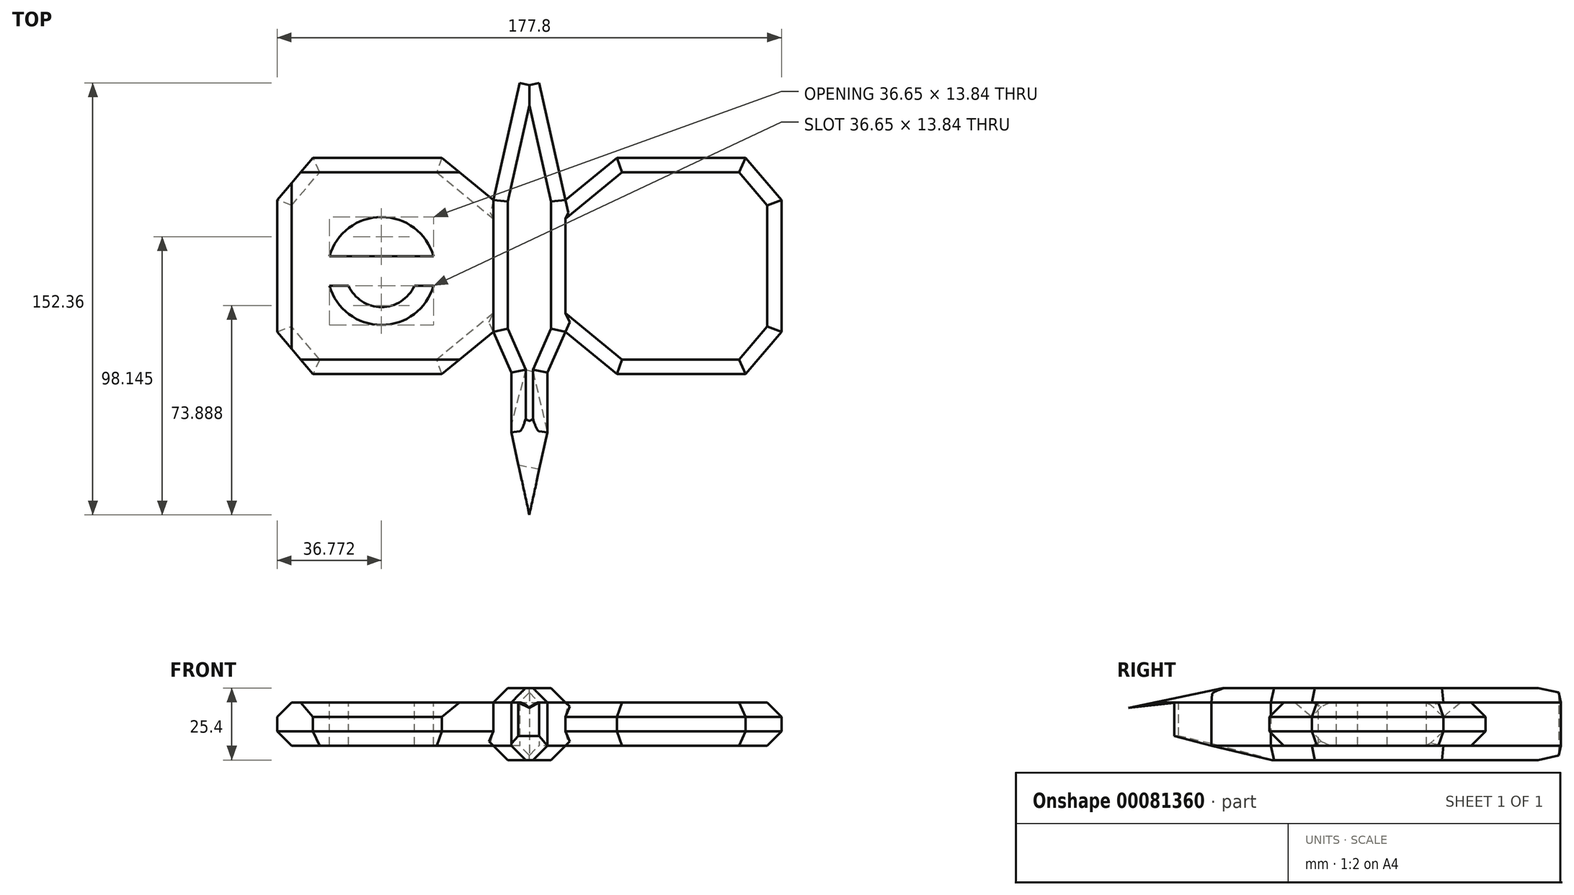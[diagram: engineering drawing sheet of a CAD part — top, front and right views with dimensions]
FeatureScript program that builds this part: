
annotation { "Feature Type Name" : "Feature", "Feature Type Description" : "" }
export const myFeature = defineFeature(function(context is Context, id is Id, definition is map)
    precondition{}
    {
        {
            var Q0;
            Q0=qCreatedBy(makeId("Top.planeOp"),FACE);
            var sketch = newSketch(context, id + "F0", { "sketchPlane" : qUnion([Q0])});
            skLineSegment(sketch, "E0", {"start": v(0, -75.69) * mm, "end": v(6.35, -46.54) * mm});
            skLineSegment(sketch, "E1", {"start": v(6.35, -46.54) * mm, "end": v(6.35, -25.5) * mm});
            skLineSegment(sketch, "E2", {"start": v(6.35, -25.5) * mm, "end": v(12.7, -11.09) * mm});
            skLineSegment(sketch, "E3", {"start": v(12.7, -11.09) * mm, "end": v(12.7, 35.35) * mm});
            skLineSegment(sketch, "E4", {"start": v(12.7, 35.35) * mm, "end": v(3.41, 76.67) * mm});
            skLineSegment(sketch, "E5", {"start": v(3.41, 76.67) * mm, "end": v(0, 75.9) * mm});
            skLineSegment(sketch, "E6", {"start": v(0, 75.9) * mm, "end": v(0, 0) * mm});
            skLineSegment(sketch, "E7", {"start": v(0, -75.69) * mm, "end": v(0, 0) * mm});
            skLineSegment(sketch, "E8", {"start": v(0, 75.9) * mm, "end": v(0, -75.69) * mm, "construction": true});
            skLineSegment(sketch, "E9", {"start": v(0, 80.35) * mm, "end": v(0, -78.48) * mm, "construction": true});
            skLineSegment(sketch, "E10.MirrorCS", {"start": v(-3.41, 76.67) * mm, "end": v(0, 75.9) * mm});
            skLineSegment(sketch, "E11.MirrorCS", {"start": v(-12.7, 35.35) * mm, "end": v(-3.41, 76.67) * mm});
            skLineSegment(sketch, "E12.MirrorCS", {"start": v(-12.7, -11.09) * mm, "end": v(-12.7, 35.35) * mm});
            skLineSegment(sketch, "E13.MirrorCS", {"start": v(-6.35, -25.5) * mm, "end": v(-12.7, -11.09) * mm});
            skLineSegment(sketch, "E14.MirrorCS", {"start": v(-6.35, -46.54) * mm, "end": v(-6.35, -25.5) * mm});
            skLineSegment(sketch, "E15.MirrorCS", {"start": v(0, -75.69) * mm, "end": v(-6.35, -46.54) * mm});
            skSolve(sketch);
        }
        {
            var Q0;
            Q0 = qSketchRegion(id + "F0", true);
            extrude(context, id + "F1", {"entities" : qUnion([Q0]), "depth" : 25.4 * mm});
        }
        {
            var Q0;
            Q0=makeQuery(id+"F1.opExtrude","CAP_EDGE",EDGE,{"disambiguationData":[OSD([sQuery(id+"F0.wireOp",EDGE,"E12.MirrorCS")])],"isStart":false});
            var Q1;
            Q1=makeQuery(id+"F1.opExtrude","CAP_EDGE",EDGE,{"disambiguationData":[OSD([sQuery(id+"F0.wireOp",EDGE,"E3")])],"isStart":false});
            var Q2;
            Q2=makeQuery(id+"F1.opExtrude","CAP_EDGE",EDGE,{"disambiguationData":[OSD([sQuery(id+"F0.wireOp",EDGE,"E12.MirrorCS")])],"isStart":true});
            var Q3;
            Q3=makeQuery(id+"F1.opExtrude","CAP_EDGE",EDGE,{"disambiguationData":[OSD([sQuery(id+"F0.wireOp",EDGE,"E3")])],"isStart":true});
            var Q4;
            Q4=makeQuery(id+"F1.opExtrude","CAP_FACE",FACE,{"disambiguationData":[OSD([sQuery(id+"F0.wireOp",EDGE,"E0"),sQuery(id+"F0.wireOp",EDGE,"E1"),sQuery(id+"F0.wireOp",EDGE,"E2"),sQuery(id+"F0.wireOp",EDGE,"E3"),sQuery(id+"F0.wireOp",EDGE,"E4"),sQuery(id+"F0.wireOp",EDGE,"E5"),sQuery(id+"F0.wireOp",EDGE,"E10.MirrorCS"),sQuery(id+"F0.wireOp",EDGE,"E11.MirrorCS"),sQuery(id+"F0.wireOp",EDGE,"E12.MirrorCS"),sQuery(id+"F0.wireOp",EDGE,"E13.MirrorCS"),sQuery(id+"F0.wireOp",EDGE,"E14.MirrorCS"),sQuery(id+"F0.wireOp",EDGE,"E15.MirrorCS")])],"isStart":true});
            var Q5;
            Q5=makeQuery(id+"F1.opExtrude","CAP_FACE",FACE,{"disambiguationData":[OSD([sQuery(id+"F0.wireOp",EDGE,"E0"),sQuery(id+"F0.wireOp",EDGE,"E1"),sQuery(id+"F0.wireOp",EDGE,"E2"),sQuery(id+"F0.wireOp",EDGE,"E3"),sQuery(id+"F0.wireOp",EDGE,"E4"),sQuery(id+"F0.wireOp",EDGE,"E5"),sQuery(id+"F0.wireOp",EDGE,"E10.MirrorCS"),sQuery(id+"F0.wireOp",EDGE,"E11.MirrorCS"),sQuery(id+"F0.wireOp",EDGE,"E12.MirrorCS"),sQuery(id+"F0.wireOp",EDGE,"E13.MirrorCS"),sQuery(id+"F0.wireOp",EDGE,"E14.MirrorCS"),sQuery(id+"F0.wireOp",EDGE,"E15.MirrorCS")])],"isStart":false});
            chamfer(context, id + "F2", {"entities" : qUnion([Q0, Q1, Q2, Q3, Q4, Q5]), "width" : 5.08 * mm, "tangentPropagation" : true});
        }
        {
            var Q0;
            Q0=makeQuery(id+"F1.opExtrude","SWEPT_FACE",FACE,{"disambiguationData":[OSD([sQuery(id+"F0.wireOp",EDGE,"E12.MirrorCS")])]});
            var sketch = newSketch(context, id + "F3", { "sketchPlane" : qUnion([Q0])});
            skLineSegment(sketch, "E16.bottom", {"start": v(25.97, 20.32) * mm, "end": v(-50.23, 20.32) * mm});
            skLineSegment(sketch, "E16.top", {"start": v(25.97, 5.08) * mm, "end": v(-50.23, 5.08) * mm});
            skLineSegment(sketch, "E16.left", {"start": v(25.97, 20.32) * mm, "end": v(25.97, 5.08) * mm});
            skLineSegment(sketch, "E16.right", {"start": v(-50.23, 20.32) * mm, "end": v(-50.23, 5.08) * mm});
            skPoint(sketch, "E16.middle", {"position": v(-12.13, 12.7) * mm});
            skPoint(sketch, "E16.middle.positionSnap0", {"position": v(11.09, 12.7) * mm});
            skPoint(sketch, "E16.middle.positionSnap1", {"position": v(-12.13, 20.32) * mm});
            skPoint(sketch, "E16.cornerSnap0", {"position": v(-12.13, 20.32) * mm});
            skPoint(sketch, "E16.centerSnap0", {"position": v(11.09, 12.7) * mm});
            skPoint(sketch, "E16.centerSnap1", {"position": v(-12.13, 20.32) * mm});
            skSolve(sketch);
        }
        {
            var Q0;
            Q0 = qSketchRegion(id + "F3", true);
            extrude(context, id + "F4", {"entities" : qUnion([Q0]), "operationType" : NewBodyOperationType.ADD, "depth" : 76.2 * mm});
        }
        {
            var Q0;
            Q0=makeQuery(id+"F4.opExtrude","SWEPT_FACE",FACE,{"disambiguationData":[OSD([sQuery(id+"F3.wireOp",EDGE,"E16.bottom")])]});
            var sketch = newSketch(context, id + "F5", { "sketchPlane" : qUnion([Q0])});
            skLineSegment(sketch, "E17", {"start": v(-30.86, 50.23) * mm, "end": v(-12.7, 35.35) * mm});
            skLineSegment(sketch, "E18", {"start": v(-12.7, 35.35) * mm, "end": v(-12.7, -11.09) * mm});
            skLineSegment(sketch, "E19", {"start": v(-12.7, -11.09) * mm, "end": v(-30.86, -25.97) * mm});
            skLineSegment(sketch, "E20", {"start": v(-30.86, -25.97) * mm, "end": v(-76.26, -25.97) * mm});
            skLineSegment(sketch, "E21", {"start": v(-76.26, -25.97) * mm, "end": v(-88.9, -11.09) * mm});
            skLineSegment(sketch, "E22", {"start": v(-88.9, -11.09) * mm, "end": v(-88.9, 35.35) * mm});
            skLineSegment(sketch, "E23", {"start": v(-88.9, 35.35) * mm, "end": v(-76.26, 50.23) * mm});
            skLineSegment(sketch, "E24", {"start": v(-76.26, 50.23) * mm, "end": v(-30.86, 50.23) * mm});
            skLineSegment(sketch, "E25", {"start": v(0, 76.7) * mm, "end": v(0, -76.41) * mm, "construction": true});
            skLineSegment(sketch, "E26.MirrorCS", {"start": v(30.86, 50.23) * mm, "end": v(12.7, 35.35) * mm});
            skLineSegment(sketch, "E27.MirrorCS", {"start": v(76.26, 50.23) * mm, "end": v(30.86, 50.23) * mm});
            skLineSegment(sketch, "E28.MirrorCS", {"start": v(88.9, 35.35) * mm, "end": v(76.26, 50.23) * mm});
            skLineSegment(sketch, "E29.MirrorCS", {"start": v(76.26, -25.97) * mm, "end": v(88.9, -11.09) * mm});
            skLineSegment(sketch, "E30.MirrorCS", {"start": v(12.7, -11.09) * mm, "end": v(30.86, -25.97) * mm});
            skLineSegment(sketch, "E31.MirrorCS", {"start": v(12.7, 35.35) * mm, "end": v(12.7, -11.09) * mm});
            skLineSegment(sketch, "E32.MirrorCS", {"start": v(88.9, -11.09) * mm, "end": v(88.9, 35.35) * mm});
            skLineSegment(sketch, "E33.MirrorCS", {"start": v(30.86, -25.97) * mm, "end": v(76.26, -25.97) * mm});
            skSolve(sketch);
        }
        {
            var Q0;
            {var subQ0=sQuery(id+"F5.wireOp",EDGE,"E23");Q0=makeQuery(id+"F5.imprint","IMPRINT",FACE,{"disambiguationData":[TD([[makeQuery(id+"F5.imprint","IMPRINT",EDGE,{"derivedFrom":subQ0}),1.0]])]});}
            var Q1;
            {var subQ0=sQuery(id+"F5.wireOp",EDGE,"E17");Q1=makeQuery(id+"F5.imprint","IMPRINT",FACE,{"disambiguationData":[TD([[makeQuery(id+"F5.imprint","IMPRINT",EDGE,{"derivedFrom":subQ0}),1.0]])]});}
            var Q2;
            {var subQ0=sQuery(id+"F5.wireOp",EDGE,"E19");Q2=makeQuery(id+"F5.imprint","IMPRINT",FACE,{"disambiguationData":[TD([[makeQuery(id+"F5.imprint","IMPRINT",EDGE,{"derivedFrom":subQ0}),1.0]])]});}
            var Q3;
            {var subQ0=sQuery(id+"F5.wireOp",EDGE,"E21");Q3=makeQuery(id+"F5.imprint","IMPRINT",FACE,{"disambiguationData":[TD([[makeQuery(id+"F5.imprint","IMPRINT",EDGE,{"derivedFrom":subQ0}),1.0]])]});}
            extrude(context, id + "F6", {"entities" : qUnion([Q0, Q1, Q2, Q3]), "operationType" : NewBodyOperationType.REMOVE, "oppositeDirection" : true, "depth" : 25.4 * mm});
        }
        {
            var Q0;
            Q0=makeQuery(id+"F1.opExtrude","SWEPT_FACE",FACE,{"disambiguationData":[OSD([sQuery(id+"F0.wireOp",EDGE,"E0")])]});
            var sketch = newSketch(context, id + "F7", { "sketchPlane" : qUnion([Q0])});
            skLineSegment(sketch, "E34", {"start": v(-73.95, 12.7) * mm, "end": v(-44.12, 5.08) * mm});
            skLineSegment(sketch, "E35", {"start": v(-44.12, 5.08) * mm, "end": v(-21.55, -0.68) * mm});
            skLineSegment(sketch, "E36", {"start": v(-21.55, -0.68) * mm, "end": v(-74.55, 0) * mm});
            skLineSegment(sketch, "E37", {"start": v(-74.55, 0) * mm, "end": v(-73.95, 12.7) * mm});
            skSolve(sketch);
        }
        {
            var Q0;
            Q0 = qSketchRegion(id + "F7", true);
            extrude(context, id + "F8", {"entities" : qUnion([Q0]), "operationType" : NewBodyOperationType.REMOVE, "oppositeDirection" : true, "depth" : 25.4 * mm});
        }
        {
            var Q0;
            Q0=makeQuery(id+"F2.opChamfer","BLEND_EDGE",EDGE,{"blendedFrom":[makeQuery(id+"F1.opExtrude","CAP_EDGE",EDGE,{"disambiguationData":[OSD([sQuery(id+"F0.wireOp",EDGE,"E0")])],"isStart":false}),makeQuery(id+"F1.opExtrude","CAP_EDGE",EDGE,{"disambiguationData":[OSD([sQuery(id+"F0.wireOp",EDGE,"E15.MirrorCS")])],"isStart":false})],"blendedInto":[]});
            fillet(context, id + "F9", {"entities" : qUnion([Q0]), "radius" : 5.08 * mm, "tangentPropagation" : true, "allowEdgeOverflow" : false});
        }
        {
            var Q0;
            Q0=makeQuery(id+"F1.opExtrude","SWEPT_FACE",FACE,{"disambiguationData":[OSD([sQuery(id+"F0.wireOp",EDGE,"E0")])]});
            var sketch = newSketch(context, id + "F10", { "sketchPlane" : qUnion([Q0])});
            skLineSegment(sketch, "E38", {"start": v(-57.46, 20.32) * mm, "end": v(-57.46, 8.49) * mm});
            skLineSegment(sketch, "E39", {"start": v(-57.46, 8.49) * mm, "end": v(-73.95, 12.7) * mm});
            skLineSegment(sketch, "E40", {"start": v(-73.95, 12.7) * mm, "end": v(-73.95, 18.33) * mm});
            skLineSegment(sketch, "E41", {"start": v(-73.95, 18.33) * mm, "end": v(-57.46, 20.32) * mm});
            skSolve(sketch);
        }
        {
            var Q0;
            Q0 = qSketchRegion(id + "F10", true);
            extrude(context, id + "F11", {"entities" : qUnion([Q0]), "operationType" : NewBodyOperationType.REMOVE, "oppositeDirection" : true, "depth" : 25.4 * mm});
        }
        {
            var Q0;
            Q0=makeQuery(id+"F4.opExtrude","SWEPT_EDGE",EDGE,{"disambiguationData":[OSD([sQuery(id+"F3.wireOp",EDGE,"E16.bottom"),sQuery(id+"F3.wireOp",EDGE,"E16.left")])]});
            var Q1;
            Q1=makeQuery(id+"F6.boolean.opBoolean","COPY",EDGE,{"derivedFrom":makeQuery(id+"F6.opExtrude","CAP_EDGE",EDGE,{"disambiguationData":[OSD([sQuery(id+"F5.wireOp",EDGE,"E21")])],"isStart":true})});
            var Q2;
            Q2=makeQuery(id+"F6.boolean.opBoolean","COPY",EDGE,{"derivedFrom":makeQuery(id+"F6.opExtrude","CAP_EDGE",EDGE,{"disambiguationData":[OSD([sQuery(id+"F5.wireOp",EDGE,"E19")])],"isStart":true})});
            var Q3;
            Q3=makeQuery(id+"F6.boolean.opBoolean","COPY",EDGE,{"derivedFrom":makeQuery(id+"F6.opExtrude","CAP_EDGE",EDGE,{"disambiguationData":[OSD([sQuery(id+"F5.wireOp",EDGE,"E17")])],"isStart":true})});
            var Q4;
            Q4=makeQuery(id+"F4.opExtrude","SWEPT_EDGE",EDGE,{"disambiguationData":[OSD([sQuery(id+"F3.wireOp",EDGE,"E16.bottom"),sQuery(id+"F3.wireOp",EDGE,"E16.right")])]});
            var Q5;
            Q5=makeQuery(id+"F6.boolean.opBoolean","COPY",EDGE,{"derivedFrom":makeQuery(id+"F6.opExtrude","CAP_EDGE",EDGE,{"disambiguationData":[OSD([sQuery(id+"F5.wireOp",EDGE,"E23")])],"isStart":true})});
            var Q6;
            Q6=makeQuery(id+"F4.opExtrude","CAP_EDGE",EDGE,{"disambiguationData":[OSD([sQuery(id+"F3.wireOp",EDGE,"E16.bottom")])],"isStart":false});
            var Q7;
            Q7=makeQuery(id+"F4.opExtrude","SWEPT_EDGE",EDGE,{"disambiguationData":[OSD([sQuery(id+"F3.wireOp",EDGE,"E16.top"),sQuery(id+"F3.wireOp",EDGE,"E16.left")])]});
            var Q8;
            Q8=makeQuery(id+"F6.boolean.opBoolean","INTERSECT",EDGE,{"derivedFrom":[makeQuery(id+"F4.opExtrude","SWEPT_FACE",FACE,{"disambiguationData":[OSD([sQuery(id+"F3.wireOp",EDGE,"E16.top")])]}),makeQuery(id+"F6.opExtrude","SWEPT_FACE",FACE,{"disambiguationData":[OSD([sQuery(id+"F5.wireOp",EDGE,"E19")])]})]});
            var Q9;
            Q9=makeQuery(id+"F6.boolean.opBoolean","INTERSECT",EDGE,{"derivedFrom":[makeQuery(id+"F4.opExtrude","SWEPT_FACE",FACE,{"disambiguationData":[OSD([sQuery(id+"F3.wireOp",EDGE,"E16.top")])]}),makeQuery(id+"F6.opExtrude","SWEPT_FACE",FACE,{"disambiguationData":[OSD([sQuery(id+"F5.wireOp",EDGE,"E21")])]})]});
            var Q10;
            Q10=makeQuery(id+"F4.opExtrude","CAP_EDGE",EDGE,{"disambiguationData":[OSD([sQuery(id+"F3.wireOp",EDGE,"E16.top")])],"isStart":false});
            var Q11;
            Q11=makeQuery(id+"F6.boolean.opBoolean","INTERSECT",EDGE,{"derivedFrom":[makeQuery(id+"F4.opExtrude","SWEPT_FACE",FACE,{"disambiguationData":[OSD([sQuery(id+"F3.wireOp",EDGE,"E16.top")])]}),makeQuery(id+"F6.opExtrude","SWEPT_FACE",FACE,{"disambiguationData":[OSD([sQuery(id+"F5.wireOp",EDGE,"E23")])]})]});
            var Q12;
            Q12=makeQuery(id+"F4.opExtrude","SWEPT_EDGE",EDGE,{"disambiguationData":[OSD([sQuery(id+"F3.wireOp",EDGE,"E16.top"),sQuery(id+"F3.wireOp",EDGE,"E16.right")])]});
            var Q13;
            Q13=makeQuery(id+"F6.boolean.opBoolean","INTERSECT",EDGE,{"derivedFrom":[makeQuery(id+"F4.opExtrude","SWEPT_FACE",FACE,{"disambiguationData":[OSD([sQuery(id+"F3.wireOp",EDGE,"E16.top")])]}),makeQuery(id+"F6.opExtrude","SWEPT_FACE",FACE,{"disambiguationData":[OSD([sQuery(id+"F5.wireOp",EDGE,"E17")])]})]});
            chamfer(context, id + "F12", {"entities" : qUnion([Q0, Q1, Q2, Q3, Q4, Q5, Q6, Q7, Q8, Q9, Q10, Q11, Q12, Q13]), "width" : 5.08 * mm, "tangentPropagation" : true});
        }
        {
            var Q0;
            Q0=makeQuery(id+"F5.imprint","IMPRINT",FACE,{"disambiguationData":[TD([[makeQuery(id+"F5.imprint","IMPRINT",EDGE,{"derivedFrom":sQuery(id+"F5.wireOp",EDGE,"E26.MirrorCS")}),1.0]])]});
            extrude(context, id + "F13", {"entities" : qUnion([Q0]), "operationType" : NewBodyOperationType.ADD, "oppositeDirection" : true, "depth" : 15.24 * mm});
        }
        {
            var Q0;
            Q0=makeQuery(id+"F13.opExtrude","CAP_EDGE",EDGE,{"disambiguationData":[OSD([sQuery(id+"F5.wireOp",EDGE,"E33.MirrorCS")])],"isStart":false});
            var Q1;
            Q1=makeQuery(id+"F13.opExtrude","CAP_EDGE",EDGE,{"disambiguationData":[OSD([sQuery(id+"F5.wireOp",EDGE,"E30.MirrorCS")])],"isStart":false});
            var Q2;
            Q2=makeQuery(id+"F13.opExtrude","CAP_EDGE",EDGE,{"disambiguationData":[OSD([sQuery(id+"F5.wireOp",EDGE,"E30.MirrorCS")])],"isStart":true});
            var Q3;
            Q3=makeQuery(id+"F13.opExtrude","CAP_EDGE",EDGE,{"disambiguationData":[OSD([sQuery(id+"F5.wireOp",EDGE,"E33.MirrorCS")])],"isStart":true});
            var Q4;
            Q4=makeQuery(id+"F13.opExtrude","CAP_EDGE",EDGE,{"disambiguationData":[OSD([sQuery(id+"F5.wireOp",EDGE,"E29.MirrorCS")])],"isStart":true});
            var Q5;
            Q5=makeQuery(id+"F13.opExtrude","CAP_EDGE",EDGE,{"disambiguationData":[OSD([sQuery(id+"F5.wireOp",EDGE,"E32.MirrorCS")])],"isStart":true});
            var Q6;
            Q6=makeQuery(id+"F13.opExtrude","CAP_EDGE",EDGE,{"disambiguationData":[OSD([sQuery(id+"F5.wireOp",EDGE,"E29.MirrorCS")])],"isStart":false});
            var Q7;
            Q7=makeQuery(id+"F13.opExtrude","CAP_EDGE",EDGE,{"disambiguationData":[OSD([sQuery(id+"F5.wireOp",EDGE,"E32.MirrorCS")])],"isStart":false});
            var Q8;
            Q8=makeQuery(id+"F13.opExtrude","CAP_EDGE",EDGE,{"disambiguationData":[OSD([sQuery(id+"F5.wireOp",EDGE,"E28.MirrorCS")])],"isStart":false});
            var Q9;
            Q9=makeQuery(id+"F13.opExtrude","CAP_EDGE",EDGE,{"disambiguationData":[OSD([sQuery(id+"F5.wireOp",EDGE,"E27.MirrorCS")])],"isStart":false});
            var Q10;
            Q10=makeQuery(id+"F13.opExtrude","CAP_EDGE",EDGE,{"disambiguationData":[OSD([sQuery(id+"F5.wireOp",EDGE,"E26.MirrorCS")])],"isStart":false});
            var Q11;
            Q11=makeQuery(id+"F13.opExtrude","CAP_EDGE",EDGE,{"disambiguationData":[OSD([sQuery(id+"F5.wireOp",EDGE,"E27.MirrorCS")])],"isStart":true});
            var Q12;
            Q12=makeQuery(id+"F13.opExtrude","CAP_EDGE",EDGE,{"disambiguationData":[OSD([sQuery(id+"F5.wireOp",EDGE,"E28.MirrorCS")])],"isStart":true});
            var Q13;
            Q13=makeQuery(id+"F13.opExtrude","CAP_EDGE",EDGE,{"disambiguationData":[OSD([sQuery(id+"F5.wireOp",EDGE,"E26.MirrorCS")])],"isStart":true});
            chamfer(context, id + "F14", {"entities" : qUnion([Q0, Q1, Q2, Q3, Q4, Q5, Q6, Q7, Q8, Q9, Q10, Q11, Q12, Q13]), "width" : 5.08 * mm, "tangentPropagation" : true});
        }
        {
            var Q0;
            Q0=makeQuery(id+"F5.imprint","IMPRINT",FACE,{"disambiguationData":[TD([[makeQuery(id+"F5.imprint","IMPRINT",EDGE,{"derivedFrom":sQuery(id+"F5.wireOp",EDGE,"E17")}),-1.0]])]});
            var sketch = newSketch(context, id + "F15", { "sketchPlane" : qUnion([Q0])});
            skCircle(sketch, "E42", {"center": v(-52.13, 10.33) * mm, "radius": 19.05 * mm});
            skArc(sketch, "E43", {"start": v(-63.71, 5.12) * mm, "mid": v(-52.13, -2.37) * mm, "end": v(-40.54, 5.12) * mm});
            skLineSegment(sketch, "E44", {"start": v(-33.8, 15.53) * mm, "end": v(-70.45, 15.53) * mm});
            skLineSegment(sketch, "E45", {"start": v(-70.45, 5.12) * mm, "end": v(-33.8, 5.12) * mm});
            skArc(sketch, "E46.trimOffspring", {"start": v(-40.54, 15.53) * mm, "mid": v(-52.13, 23.03) * mm, "end": v(-63.71, 15.53) * mm});
            skLineSegment(sketch, "E47", {"start": v(-63.71, 5.12) * mm, "end": v(-70.45, 5.12) * mm});
            skLineSegment(sketch, "E48", {"start": v(-40.54, 5.12) * mm, "end": v(-33.8, 5.12) * mm});
            skLineSegment(sketch, "E49", {"start": v(-33.8, 15.53) * mm, "end": v(-40.54, 15.53) * mm});
            skLineSegment(sketch, "E50", {"start": v(-63.71, 15.53) * mm, "end": v(-70.45, 15.53) * mm});
            skLineSegment(sketch, "E51", {"start": v(-63.71, 15.53) * mm, "end": v(-40.54, 15.53) * mm});
            skLineSegment(sketch, "E52", {"start": v(-40.54, 5.12) * mm, "end": v(-63.71, 5.12) * mm});
            skLineSegment(sketch, "E53", {"start": v(-40.54, 15.53) * mm, "end": v(-63.71, 15.53) * mm});
            skLineSegment(sketch, "E54", {"start": v(-40.54, 15.53) * mm, "end": v(-33.8, 15.53) * mm});
            skSolve(sketch);
        }
        {
            var Q0;
            Q0=makeQuery(id+"F15.imprint","IMPRINT",FACE,{"disambiguationData":[TD([[makeQuery(id+"F15.imprint","IMPRINT",EDGE,{"derivedFrom":sQuery(id+"F15.wireOp",EDGE,"E46.trimOffspring")}),1.0]])]});
            var Q1;
            Q1=makeQuery(id+"F15.imprint","IMPRINT",FACE,{"disambiguationData":[TD([[makeQuery(id+"F15.imprint","IMPRINT",EDGE,{"derivedFrom":sQuery(id+"F15.wireOp",EDGE,"E46.trimOffspring")}),-1.0]])]});
            var Q2;
            Q2=makeQuery(id+"F15.imprint","IMPRINT",FACE,{"disambiguationData":[TD([[makeQuery(id+"F15.imprint","IMPRINT",EDGE,{"derivedFrom":sQuery(id+"F15.wireOp",EDGE,"E43")}),-1.0]])]});
            extrude(context, id + "F16", {"entities" : qUnion([Q0, Q1, Q2]), "operationType" : NewBodyOperationType.REMOVE, "oppositeDirection" : true, "depth" : 25.4 * mm});
        }
    });
